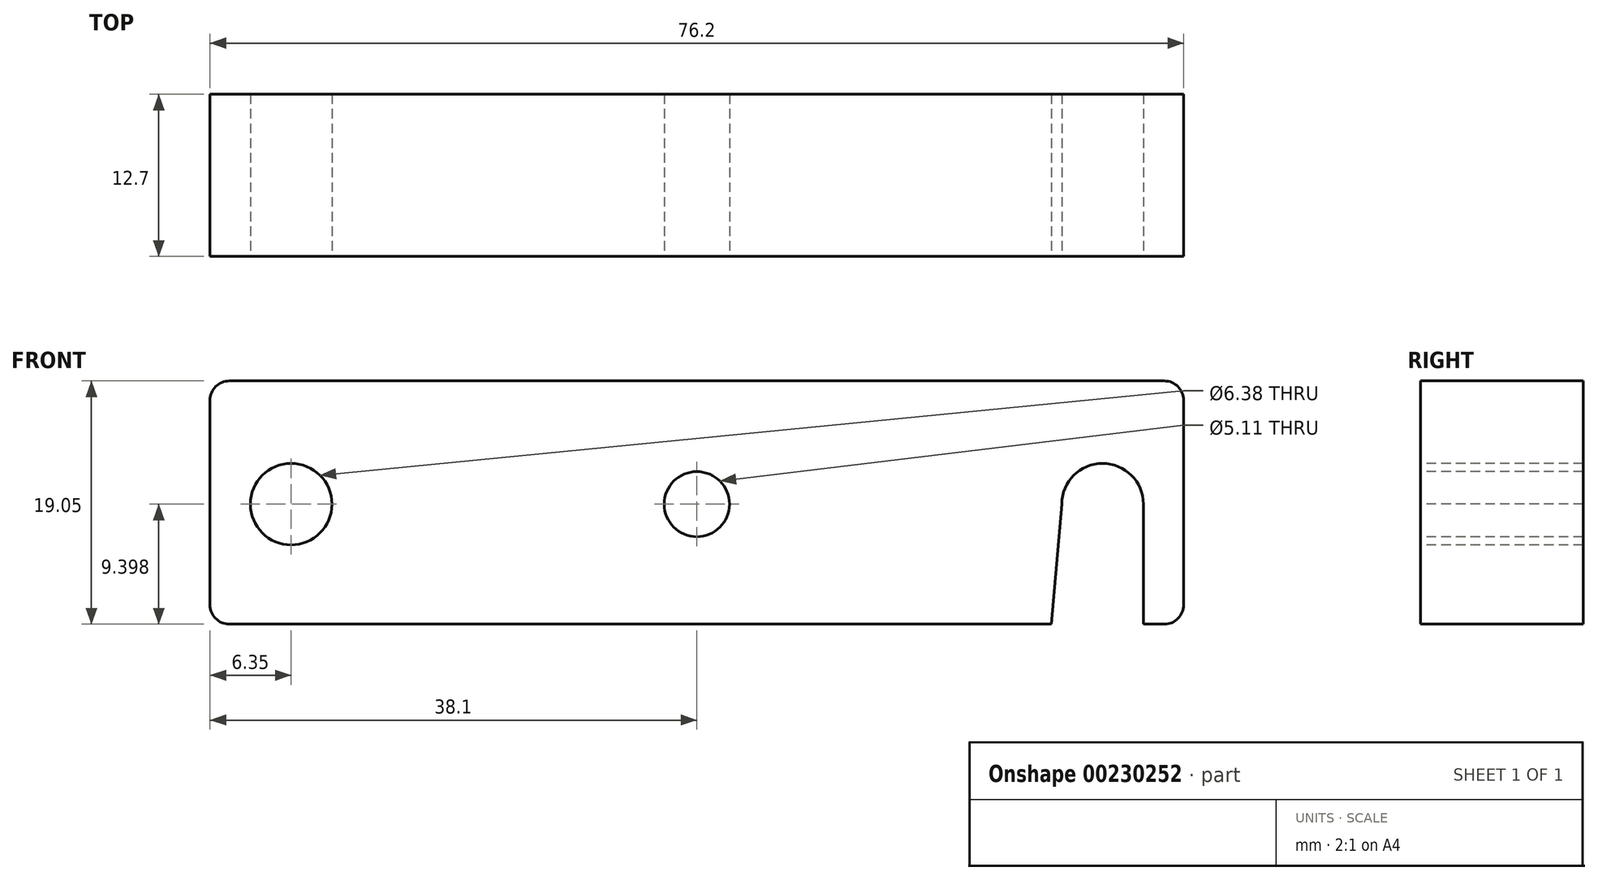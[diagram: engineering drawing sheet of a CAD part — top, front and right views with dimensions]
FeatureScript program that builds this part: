
annotation { "Feature Type Name" : "Feature", "Feature Type Description" : "" }
export const myFeature = defineFeature(function(context is Context, id is Id, definition is map)
    precondition{}
    {
        {
            var Q0;
            Q0=qCreatedBy(makeId("Right.planeOp"),FACE);
            var sketch = newSketch(context, id + "F0", { "sketchPlane" : qUnion([Q0])});
            skLineSegment(sketch, "E0.bottom", {"start": v(0, 0) * mm, "end": v(12.7, 0) * mm});
            skLineSegment(sketch, "E0.top", {"start": v(0, 19.05) * mm, "end": v(12.7, 19.05) * mm});
            skLineSegment(sketch, "E0.left", {"start": v(0, 0) * mm, "end": v(0, 19.05) * mm});
            skLineSegment(sketch, "E0.right", {"start": v(12.7, 0) * mm, "end": v(12.7, 19.05) * mm});
            skSolve(sketch);
        }
        {
            var Q0;
            Q0 = qSketchRegion(id + "F0", true);
            extrude(context, id + "F1", {"entities" : qUnion([Q0]), "depth" : 76.2 * mm});
        }
        {
            var Q0;
            Q0=makeQuery(id+"F1.opExtrude","SWEPT_FACE",FACE,{"disambiguationData":[OSD([sQuery(id+"F0.wireOp",EDGE,"E0.left")])]});
            var sketch = newSketch(context, id + "F2", { "sketchPlane" : qUnion([Q0])});
            skLineSegment(sketch, "E1", {"start": v(0, 9.4) * mm, "end": v(6.35, 9.4) * mm});
            skLineSegment(sketch, "E2", {"start": v(6.35, 9.4) * mm, "end": v(38.1, 9.4) * mm});
            skPoint(sketch, "E3", {"position": v(38.1, 9.4) * mm});
            skCircle(sketch, "E4", {"center": v(6.35, 9.4) * mm, "radius": 3.19 * mm});
            skLineSegment(sketch, "E5", {"start": v(6.35, 9.4) * mm, "end": v(69.85, 9.4) * mm});
            skArc(sketch, "E6", {"start": v(73.04, 9.4) * mm, "mid": v(69.85, 12.59) * mm, "end": v(66.66, 9.4) * mm});
            skLineSegment(sketch, "E7", {"start": v(66.66, 9.4) * mm, "end": v(65.84, 0) * mm});
            skLineSegment(sketch, "E8", {"start": v(69.85, 9.4) * mm, "end": v(69.85, 0) * mm, "construction": true});
            skLineSegment(sketch, "E9", {"start": v(73.04, 0) * mm, "end": v(73.04, 9.4) * mm});
            skSolve(sketch);
        }
        {
            var Q0;
            {var subQ0=sQuery(id+"F2.wireOp",EDGE,"E5");var subQ1=sQuery(id+"F2.wireOp",EDGE,"E1");var subQ2=makeQuery(id+"F2.imprint","INTERSECT",VERTEX,{"derivedFrom":[subQ1,subQ0]});Q0=makeQuery(id+"F2.imprint","IMPRINT",FACE,{"disambiguationData":[TD([[makeQuery(id+"F2.imprint","IMPRINT",EDGE,{"disambiguationData":[TD([[subQ2,1.0]])],"derivedFrom":subQ1}),-1.0]])]});}
            var Q1;
            Q1=makeQuery(id+"F2.imprint","IMPRINT",FACE,{"disambiguationData":[TD([[makeQuery(id+"F2.imprint","IMPRINT",EDGE,{"derivedFrom":sQuery(id+"F2.wireOp",EDGE,"E6")}),1.0]])]});
            var Q2;
            {var subQ0=sQuery(id+"F2.wireOp",EDGE,"E5");var subQ1=sQuery(id+"F2.wireOp",EDGE,"E1");var subQ2=makeQuery(id+"F2.imprint","INTERSECT",VERTEX,{"derivedFrom":[subQ1,subQ0]});Q2=makeQuery(id+"F2.imprint","IMPRINT",FACE,{"disambiguationData":[TD([[makeQuery(id+"F2.imprint","IMPRINT",EDGE,{"disambiguationData":[TD([[subQ2,1.0]])],"derivedFrom":subQ1}),1.0]])]});}
            extrude(context, id + "F3", {"entities" : qUnion([Q0, Q1, Q2]), "operationType" : NewBodyOperationType.REMOVE, "oppositeDirection" : true, "depth" : 25.4 * mm});
        }
        {
            var Q0;
            Q0=sQuery(id+"F2.wireOp",VERTEX,"E3");
            var Q1;
            Q1=makeQuery(id+"F1.opExtrude","SWEPT_BODY",BODY,{"disambiguationData":[OSD([sQuery(id+"F0.wireOp",EDGE,"E0.bottom"),sQuery(id+"F0.wireOp",EDGE,"E0.top"),sQuery(id+"F0.wireOp",EDGE,"E0.left"),sQuery(id+"F0.wireOp",EDGE,"E0.right")])]});
            hole(context, id + "F4", {"style" : HoleStyle.SIMPLE, "endStyle" : HoleEndStyle.THROUGH, "standardTappedOrClearance" : lookupTablePath({ "standard" : "ANSI", "engagement" : "75%", "pitch" : "20 tpi", "size" : "1/4", "type" : "Tapped" }), "standardBlindInLast" : lookupTablePath({ "standard" : "ANSI", "engagement" : "75%", "pitch" : "20 tpi", "size" : "1/4", "type" : "Tapped" }), "holeDiameter" : 5.1 * mm, "locations" : qUnion([Q0]), "scope" : qUnion([Q1]), "isTappedThrough" : true, "majorDiameter" : 6.35 * mm, "showTappedDepth" : true});
        }
        {
            var Q0;
            Q0=makeQuery(id+"F1.opExtrude","CAP_EDGE",EDGE,{"disambiguationData":[OSD([sQuery(id+"F0.wireOp",EDGE,"E0.top")])],"isStart":false});
            var Q1;
            Q1=makeQuery(id+"F1.opExtrude","CAP_EDGE",EDGE,{"disambiguationData":[OSD([sQuery(id+"F0.wireOp",EDGE,"E0.top")])],"isStart":true});
            var Q2;
            Q2=makeQuery(id+"F1.opExtrude","CAP_EDGE",EDGE,{"disambiguationData":[OSD([sQuery(id+"F0.wireOp",EDGE,"E0.bottom")])],"isStart":false});
            var Q3;
            Q3=makeQuery(id+"F1.opExtrude","CAP_EDGE",EDGE,{"disambiguationData":[OSD([sQuery(id+"F0.wireOp",EDGE,"E0.bottom")])],"isStart":true});
            fillet(context, id + "F5", {"entities" : qUnion([Q0, Q1, Q2, Q3]), "radius" : 1.52 * mm, "tangentPropagation" : true, "allowEdgeOverflow" : false});
        }
    });
